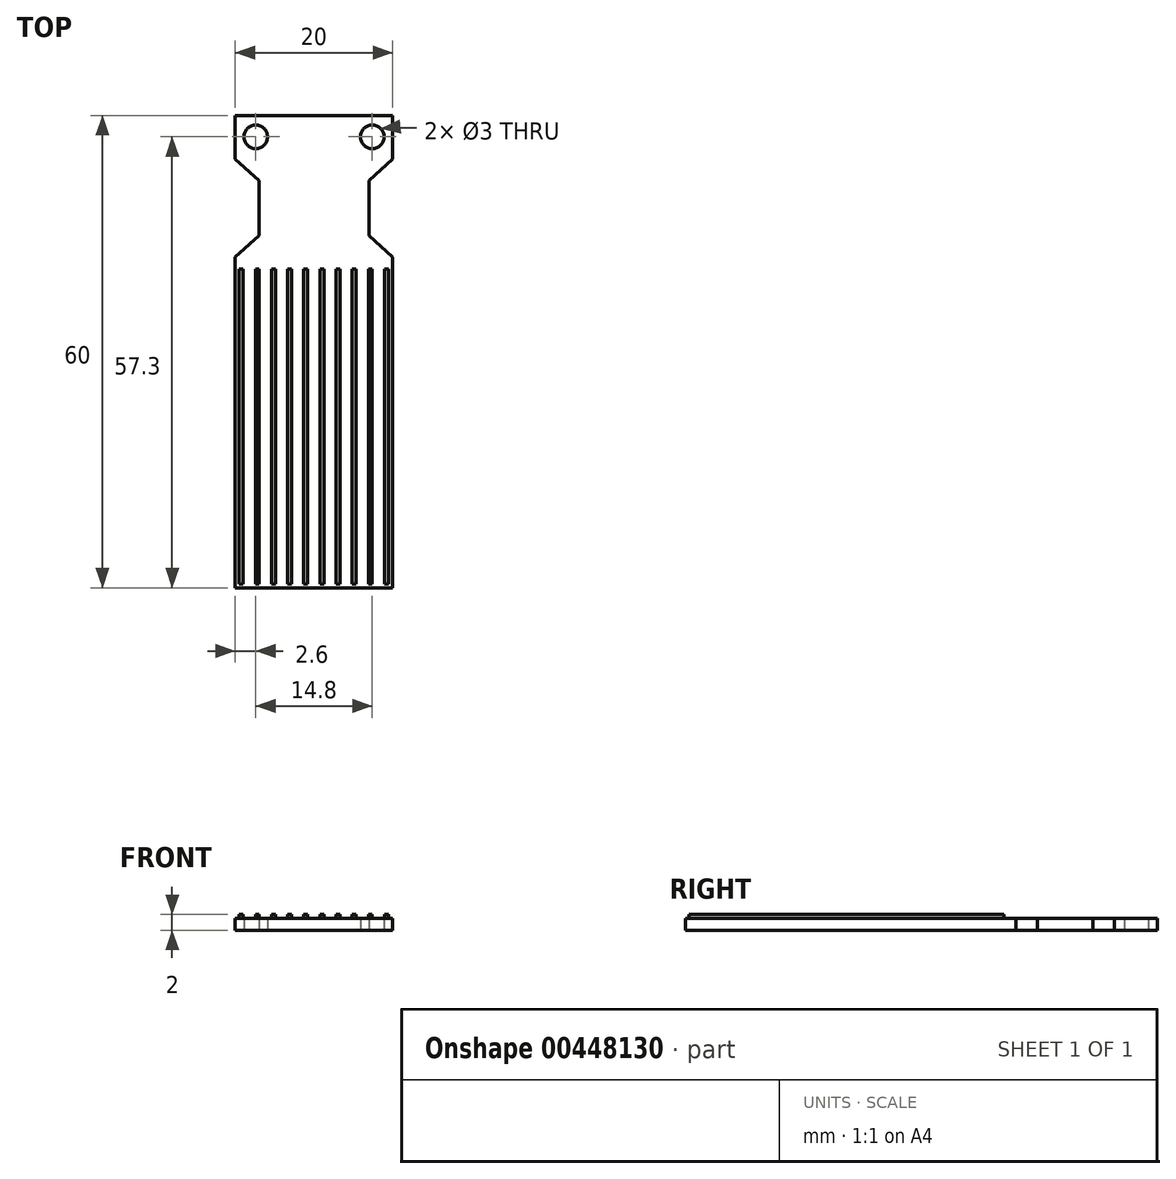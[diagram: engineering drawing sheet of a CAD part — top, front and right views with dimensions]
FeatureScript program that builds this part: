
annotation { "Feature Type Name" : "Feature", "Feature Type Description" : "" }
export const myFeature = defineFeature(function(context is Context, id is Id, definition is map)
    precondition{}
    {
        {
            var Q0;
            Q0=qCreatedBy(makeId("Top.planeOp"),FACE);
            var sketch = newSketch(context, id + "F0", { "sketchPlane" : qUnion([Q0])});
            skLineSegment(sketch, "E0.bottom", {"start": v(10, -21) * mm, "end": v(-10, -21) * mm});
            skLineSegment(sketch, "E0.top", {"start": v(10, 21) * mm, "end": v(-10, 21) * mm});
            skLineSegment(sketch, "E0.left", {"start": v(10, -21) * mm, "end": v(10, 21) * mm});
            skLineSegment(sketch, "E0.right", {"start": v(-10, -21) * mm, "end": v(-10, 21) * mm});
            skPoint(sketch, "E0.middle", {"position": v(0, 0) * mm});
            skLineSegment(sketch, "E1", {"start": v(-10, 21) * mm, "end": v(-7, 23.75) * mm});
            skLineSegment(sketch, "E2", {"start": v(-7, 23.75) * mm, "end": v(-7, 30.75) * mm});
            skLineSegment(sketch, "E3", {"start": v(-7, 30.75) * mm, "end": v(-10, 33.5) * mm});
            skLineSegment(sketch, "E4", {"start": v(10, 33.5) * mm, "end": v(7, 30.75) * mm});
            skLineSegment(sketch, "E5", {"start": v(7, 30.75) * mm, "end": v(7, 23.75) * mm});
            skLineSegment(sketch, "E6", {"start": v(7, 23.75) * mm, "end": v(10, 21) * mm});
            skLineSegment(sketch, "E7", {"start": v(-10, 33.5) * mm, "end": v(-10, 39) * mm});
            skLineSegment(sketch, "E8", {"start": v(-10, 39) * mm, "end": v(10, 39) * mm});
            skLineSegment(sketch, "E9", {"start": v(10, 39) * mm, "end": v(10, 33.5) * mm});
            skPoint(sketch, "E10", {"position": v(0, 39) * mm});
            skPoint(sketch, "E11", {"position": v(0, 21) * mm});
            skLineSegment(sketch, "E12", {"start": v(0, 21) * mm, "end": v(0, 0) * mm, "construction": true});
            skCircle(sketch, "E13", {"center": v(-7.4, 36.3) * mm, "radius": 1.5 * mm});
            skCircle(sketch, "E14", {"center": v(7.4, 36.3) * mm, "radius": 1.5 * mm});
            skPoint(sketch, "E15", {"position": v(-8.9, 36.3) * mm});
            skPoint(sketch, "E16", {"position": v(-7.4, 37.8) * mm});
            skLineSegment(sketch, "E17", {"start": v(7.4, 36.3) * mm, "end": v(-7.4, 36.3) * mm, "construction": true});
            skPoint(sketch, "E18", {"position": v(0, 36.3) * mm});
            skSolve(sketch);
        }
        {
            var Q0;
            Q0=makeQuery(id+"F0.imprint","IMPRINT",FACE,{"disambiguationData":[TD([[makeQuery(id+"F0.imprint","IMPRINT",EDGE,{"derivedFrom":sQuery(id+"F0.wireOp",EDGE,"E0.bottom")}),-1.0]])]});
            var Q1;
            Q1=makeQuery(id+"F0.imprint","IMPRINT",FACE,{"disambiguationData":[TD([[makeQuery(id+"F0.imprint","IMPRINT",EDGE,{"derivedFrom":sQuery(id+"F0.wireOp",EDGE,"E0.top")}),-1.0]])]});
            extrude(context, id + "F1", {"entities" : qUnion([Q0, Q1]), "depth" : 1.5 * mm});
        }
        {
            var Q0;
            Q0=makeQuery(id+"F1.opExtrude","CAP_FACE",FACE,{"disambiguationData":[OSD([sQuery(id+"F0.wireOp",EDGE,"E0.bottom"),sQuery(id+"F0.wireOp",EDGE,"E0.left"),sQuery(id+"F0.wireOp",EDGE,"E0.right"),sQuery(id+"F0.wireOp",EDGE,"E1"),sQuery(id+"F0.wireOp",EDGE,"E2"),sQuery(id+"F0.wireOp",EDGE,"E3"),sQuery(id+"F0.wireOp",EDGE,"E4"),sQuery(id+"F0.wireOp",EDGE,"E5"),sQuery(id+"F0.wireOp",EDGE,"E6"),sQuery(id+"F0.wireOp",EDGE,"E7"),sQuery(id+"F0.wireOp",EDGE,"E8"),sQuery(id+"F0.wireOp",EDGE,"E9"),sQuery(id+"F0.wireOp",EDGE,"E13"),sQuery(id+"F0.wireOp",EDGE,"E14")])],"isStart":false});
            var sketch = newSketch(context, id + "F2", { "sketchPlane" : qUnion([Q0])});
            skLineSegment(sketch, "E19.bottom", {"start": v(-9.5, 19.5) * mm, "end": v(-9, 19.5) * mm});
            skLineSegment(sketch, "E19.top", {"start": v(-9.5, -20.5) * mm, "end": v(-9, -20.5) * mm});
            skLineSegment(sketch, "E19.left", {"start": v(-9.5, 19.5) * mm, "end": v(-9.5, -20.5) * mm});
            skLineSegment(sketch, "E19.right", {"start": v(-9, 19.5) * mm, "end": v(-9, -20.5) * mm});
            skLineSegment(sketch, "E20.1.0.0", {"start": v(-7.45, 19.5) * mm, "end": v(-6.95, 19.5) * mm});
            skLineSegment(sketch, "E20.1.0.1", {"start": v(-7.45, 19.5) * mm, "end": v(-7.45, -20.5) * mm});
            skLineSegment(sketch, "E20.1.0.2", {"start": v(-6.95, 19.5) * mm, "end": v(-6.95, -20.5) * mm});
            skLineSegment(sketch, "E20.1.0.3", {"start": v(-7.45, -20.5) * mm, "end": v(-6.95, -20.5) * mm});
            skLineSegment(sketch, "E20.2.0.0", {"start": v(-5.4, 19.5) * mm, "end": v(-4.9, 19.5) * mm});
            skLineSegment(sketch, "E20.2.0.1", {"start": v(-5.4, 19.5) * mm, "end": v(-5.4, -20.5) * mm});
            skLineSegment(sketch, "E20.2.0.2", {"start": v(-4.9, 19.5) * mm, "end": v(-4.9, -20.5) * mm});
            skLineSegment(sketch, "E20.2.0.3", {"start": v(-5.4, -20.5) * mm, "end": v(-4.9, -20.5) * mm});
            skLineSegment(sketch, "E20.3.0.0", {"start": v(-3.35, 19.5) * mm, "end": v(-2.85, 19.5) * mm});
            skLineSegment(sketch, "E20.3.0.1", {"start": v(-3.35, 19.5) * mm, "end": v(-3.35, -20.5) * mm});
            skLineSegment(sketch, "E20.3.0.2", {"start": v(-2.85, 19.5) * mm, "end": v(-2.85, -20.5) * mm});
            skLineSegment(sketch, "E20.3.0.3", {"start": v(-3.35, -20.5) * mm, "end": v(-2.85, -20.5) * mm});
            skLineSegment(sketch, "E20.4.0.0", {"start": v(-1.3, 19.5) * mm, "end": v(-0.8, 19.5) * mm});
            skLineSegment(sketch, "E20.4.0.1", {"start": v(-1.3, 19.5) * mm, "end": v(-1.3, -20.5) * mm});
            skLineSegment(sketch, "E20.4.0.2", {"start": v(-0.8, 19.5) * mm, "end": v(-0.8, -20.5) * mm});
            skLineSegment(sketch, "E20.4.0.3", {"start": v(-1.3, -20.5) * mm, "end": v(-0.8, -20.5) * mm});
            skLineSegment(sketch, "E20.5.0.0", {"start": v(0.75, 19.5) * mm, "end": v(1.25, 19.5) * mm});
            skLineSegment(sketch, "E20.5.0.1", {"start": v(0.75, 19.5) * mm, "end": v(0.75, -20.5) * mm});
            skLineSegment(sketch, "E20.5.0.2", {"start": v(1.25, 19.5) * mm, "end": v(1.25, -20.5) * mm});
            skLineSegment(sketch, "E20.5.0.3", {"start": v(0.75, -20.5) * mm, "end": v(1.25, -20.5) * mm});
            skLineSegment(sketch, "E20.6.0.0", {"start": v(2.8, 19.5) * mm, "end": v(3.3, 19.5) * mm});
            skLineSegment(sketch, "E20.6.0.1", {"start": v(2.8, 19.5) * mm, "end": v(2.8, -20.5) * mm});
            skLineSegment(sketch, "E20.6.0.2", {"start": v(3.3, 19.5) * mm, "end": v(3.3, -20.5) * mm});
            skLineSegment(sketch, "E20.6.0.3", {"start": v(2.8, -20.5) * mm, "end": v(3.3, -20.5) * mm});
            skLineSegment(sketch, "E20.7.0.0", {"start": v(4.85, 19.5) * mm, "end": v(5.35, 19.5) * mm});
            skLineSegment(sketch, "E20.7.0.1", {"start": v(4.85, 19.5) * mm, "end": v(4.85, -20.5) * mm});
            skLineSegment(sketch, "E20.7.0.2", {"start": v(5.35, 19.5) * mm, "end": v(5.35, -20.5) * mm});
            skLineSegment(sketch, "E20.7.0.3", {"start": v(4.85, -20.5) * mm, "end": v(5.35, -20.5) * mm});
            skLineSegment(sketch, "E20.8.0.0", {"start": v(6.9, 19.5) * mm, "end": v(7.4, 19.5) * mm});
            skLineSegment(sketch, "E20.8.0.1", {"start": v(6.9, 19.5) * mm, "end": v(6.9, -20.5) * mm});
            skLineSegment(sketch, "E20.8.0.2", {"start": v(7.4, 19.5) * mm, "end": v(7.4, -20.5) * mm});
            skLineSegment(sketch, "E20.8.0.3", {"start": v(6.9, -20.5) * mm, "end": v(7.4, -20.5) * mm});
            skLineSegment(sketch, "E20.9.0.0", {"start": v(8.95, 19.5) * mm, "end": v(9.45, 19.5) * mm});
            skLineSegment(sketch, "E20.9.0.1", {"start": v(8.95, 19.5) * mm, "end": v(8.95, -20.5) * mm});
            skLineSegment(sketch, "E20.9.0.2", {"start": v(9.45, 19.5) * mm, "end": v(9.45, -20.5) * mm});
            skLineSegment(sketch, "E20.9.0.3", {"start": v(8.95, -20.5) * mm, "end": v(9.45, -20.5) * mm});
            skLineSegment(sketch, "E20.direction1", {"start": v(-9.5, -20.5) * mm, "end": v(-7.45, -20.5) * mm, "construction": true});
            skSolve(sketch);
        }
        {
            var Q0;
            Q0=makeQuery(id+"F2.imprint","IMPRINT",FACE,{"disambiguationData":[TD([[makeQuery(id+"F2.imprint","IMPRINT",EDGE,{"derivedFrom":sQuery(id+"F2.wireOp",EDGE,"E19.bottom")}),-1.0]])]});
            var Q1;
            Q1=makeQuery(id+"F2.imprint","IMPRINT",FACE,{"disambiguationData":[TD([[makeQuery(id+"F2.imprint","IMPRINT",EDGE,{"derivedFrom":sQuery(id+"F2.wireOp",EDGE,"E20.1.0.0")}),-1.0]])]});
            var Q2;
            Q2=makeQuery(id+"F2.imprint","IMPRINT",FACE,{"disambiguationData":[TD([[makeQuery(id+"F2.imprint","IMPRINT",EDGE,{"derivedFrom":sQuery(id+"F2.wireOp",EDGE,"E20.2.0.0")}),-1.0]])]});
            var Q3;
            Q3=makeQuery(id+"F2.imprint","IMPRINT",FACE,{"disambiguationData":[TD([[makeQuery(id+"F2.imprint","IMPRINT",EDGE,{"derivedFrom":sQuery(id+"F2.wireOp",EDGE,"E20.3.0.0")}),-1.0]])]});
            var Q4;
            Q4=makeQuery(id+"F2.imprint","IMPRINT",FACE,{"disambiguationData":[TD([[makeQuery(id+"F2.imprint","IMPRINT",EDGE,{"derivedFrom":sQuery(id+"F2.wireOp",EDGE,"E20.4.0.0")}),-1.0]])]});
            var Q5;
            Q5=makeQuery(id+"F2.imprint","IMPRINT",FACE,{"disambiguationData":[TD([[makeQuery(id+"F2.imprint","IMPRINT",EDGE,{"derivedFrom":sQuery(id+"F2.wireOp",EDGE,"E20.5.0.0")}),-1.0]])]});
            var Q6;
            Q6=makeQuery(id+"F2.imprint","IMPRINT",FACE,{"disambiguationData":[TD([[makeQuery(id+"F2.imprint","IMPRINT",EDGE,{"derivedFrom":sQuery(id+"F2.wireOp",EDGE,"E20.6.0.0")}),-1.0]])]});
            var Q7;
            Q7=makeQuery(id+"F2.imprint","IMPRINT",FACE,{"disambiguationData":[TD([[makeQuery(id+"F2.imprint","IMPRINT",EDGE,{"derivedFrom":sQuery(id+"F2.wireOp",EDGE,"E20.7.0.0")}),-1.0]])]});
            var Q8;
            Q8=makeQuery(id+"F2.imprint","IMPRINT",FACE,{"disambiguationData":[TD([[makeQuery(id+"F2.imprint","IMPRINT",EDGE,{"derivedFrom":sQuery(id+"F2.wireOp",EDGE,"E20.8.0.0")}),-1.0]])]});
            var Q9;
            Q9=makeQuery(id+"F2.imprint","IMPRINT",FACE,{"disambiguationData":[TD([[makeQuery(id+"F2.imprint","IMPRINT",EDGE,{"derivedFrom":sQuery(id+"F2.wireOp",EDGE,"E20.9.0.0")}),-1.0]])]});
            extrude(context, id + "F3", {"entities" : qUnion([Q0, Q1, Q2, Q3, Q4, Q5, Q6, Q7, Q8, Q9]), "operationType" : NewBodyOperationType.ADD, "depth" : .5 * mm});
        }
    });
